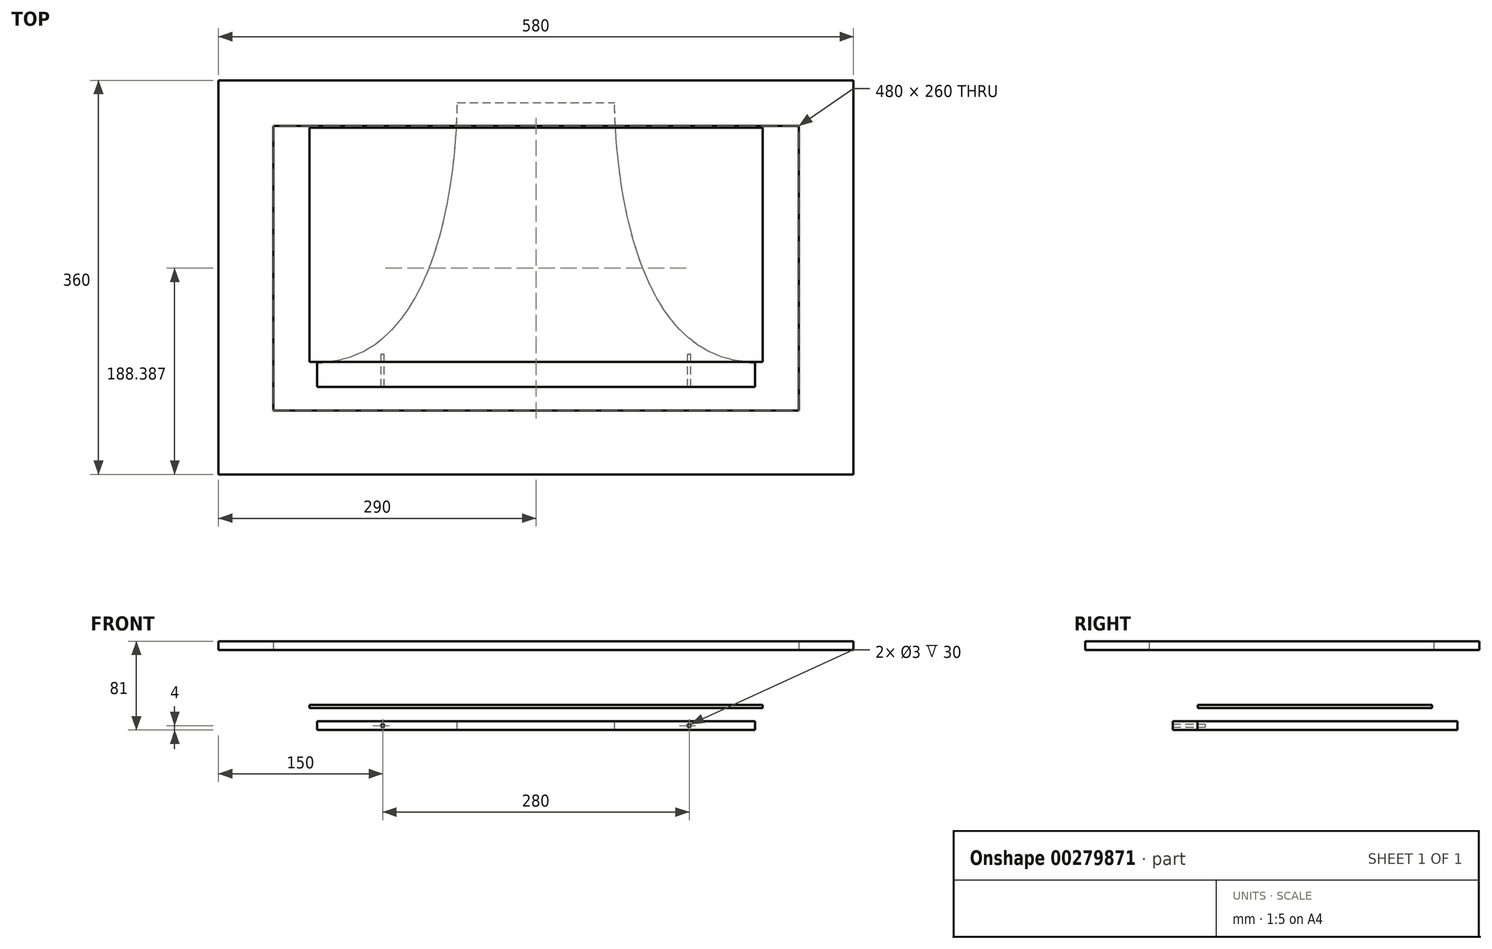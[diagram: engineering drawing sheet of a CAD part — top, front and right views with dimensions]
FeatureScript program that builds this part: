
annotation { "Feature Type Name" : "Feature", "Feature Type Description" : "" }
export const myFeature = defineFeature(function(context is Context, id is Id, definition is map)
    precondition{}
    {
        {
            var Q0;
            Q0=qCreatedBy(makeId("Top.planeOp"),FACE);
            var sketch = newSketch(context, id + "F0", { "sketchPlane" : qUnion([Q0])});
            skLineSegment(sketch, "E0.bottom", {"start": v(0, 0) * mm, "end": v(400, 0) * mm, "construction": true});
            skLineSegment(sketch, "E0.top", {"start": v(0, 200) * mm, "end": v(400, 200) * mm, "construction": true});
            skLineSegment(sketch, "E0.left", {"start": v(0, 0) * mm, "end": v(0, 200) * mm, "construction": true});
            skLineSegment(sketch, "E0.right", {"start": v(400, 0) * mm, "end": v(400, 200) * mm, "construction": true});
            skLineSegment(sketch, "E1.0", {"start": v(-7, -7) * mm, "end": v(-7, 207) * mm});
            skLineSegment(sketch, "E1.1", {"start": v(-7, -7) * mm, "end": v(407, -7) * mm});
            skLineSegment(sketch, "E1.2", {"start": v(407, -7) * mm, "end": v(407, 207) * mm});
            skLineSegment(sketch, "E1.3", {"start": v(-7, 207) * mm, "end": v(407, 207) * mm});
            skSolve(sketch);
        }
        {
            var Q0;
            Q0 = qSketchRegion(id + "F0", true);
            extrude(context, id + "F1", {"entities" : qUnion([Q0]), "oppositeDirection" : true, "depth" : 3 * mm});
        }
        {
            var Q0;
            Q0=qCreatedBy(makeId("Top.planeOp"),FACE);
            cPlane(context, id + "F2", {"entities" : qUnion([Q0]), "cplaneType" : CPlaneType.OFFSET, "offset" : 15 * mm, "oppositeDirection" : true, "width" : 150 * mm, "height" : 150 * mm});
        }
        {
            var Q0;
            Q0=qCreatedBy(id+"F2.planeOp",FACE);
            var sketch = newSketch(context, id + "F3", { "sketchPlane" : qUnion([Q0])});
            skLineSegment(sketch, "E2", {"start": v(200, 233.83) * mm, "end": v(200, -32.05) * mm, "construction": true});
            skLineSegment(sketch, "E3", {"start": v(0, -30) * mm, "end": v(0, -7.26) * mm});
            skLineSegment(sketch, "E4", {"start": v(0, -30) * mm, "end": v(400, -30) * mm});
            skLineSegment(sketch, "E5", {"start": v(400, -30) * mm, "end": v(400, -7.26) * mm});
            skLineSegment(sketch, "E6", {"start": v(128.1, 230) * mm, "end": v(271.9, 230) * mm});
            skFitSpline(sketch, "E7", {"points": [v(0, -7.26) * mm, v(128.1, 230) * mm], "startDerivative": vector(361.88, 0) * mm, "endDerivative": vector(0, 104.18) * mm});
            skFitSpline(sketch, "E8.MirrorCS", {"points": [v(400, -7.26) * mm, v(271.9, 230) * mm], "startDerivative": vector(-361.88, 0) * mm, "endDerivative": vector(0, 104.18) * mm});
            skSolve(sketch);
        }
        {
            var Q0;
            Q0 = qSketchRegion(id + "F3", true);
            extrude(context, id + "F4", {"entities" : qUnion([Q0]), "oppositeDirection" : true, "depth" : 8 * mm});
        }
        {
            var Q0;
            Q0=qCreatedBy(makeId("Front.planeOp"),FACE);
            var sketch = newSketch(context, id + "F5", { "sketchPlane" : qUnion([Q0])});
            skCircle(sketch, "E9", {"center": v(340, -19) * mm, "radius": 1.5 * mm});
            skCircle(sketch, "E10", {"center": v(60, -19) * mm, "radius": 1.5 * mm});
            skLineSegment(sketch, "E11", {"start": v(340, -19) * mm, "end": v(60, -19) * mm, "construction": true});
            skLineSegment(sketch, "E12", {"start": v(200, -15) * mm, "end": v(200, -23) * mm});
            skPoint(sketch, "E13", {"position": v(200, -19) * mm});
            skSolve(sketch);
        }
        {
            var Q0;
            Q0 = qSketchRegion(id + "F5", true);
            extrude(context, id + "F6", {"entities" : qUnion([Q0]), "operationType" : NewBodyOperationType.REMOVE, "endBound" : BoundingType.THROUGH_ALL, "depth" : 25 * mm});
        }
        {
            var Q0;
            Q0=qCreatedBy(makeId("Top.planeOp"),FACE);
            cPlane(context, id + "F7", {"entities" : qUnion([Q0]), "cplaneType" : CPlaneType.OFFSET, "offset" : 50 * mm, "width" : 150 * mm, "height" : 150 * mm});
        }
        {
            var Q0;
            Q0=qCreatedBy(id+"F7.planeOp",FACE);
            var sketch = newSketch(context, id + "F8", { "sketchPlane" : qUnion([Q0])});
            skLineSegment(sketch, "E14", {"start": v(200, 230) * mm, "end": v(200, -30) * mm, "construction": true});
            skLineSegment(sketch, "E15.bottom", {"start": v(490, 250.23) * mm, "end": v(-90, 250.23) * mm});
            skLineSegment(sketch, "E15.top", {"start": v(490, -109.77) * mm, "end": v(-90, -109.77) * mm});
            skLineSegment(sketch, "E15.left", {"start": v(490, 250.23) * mm, "end": v(490, -109.77) * mm});
            skLineSegment(sketch, "E15.right", {"start": v(-90, 250.23) * mm, "end": v(-90, -109.77) * mm});
            skPoint(sketch, "E15.middle", {"position": v(200, 70.23) * mm});
            skLineSegment(sketch, "E16.bottom", {"start": v(440, 208.62) * mm, "end": v(-40, 208.62) * mm});
            skLineSegment(sketch, "E16.top", {"start": v(440, -51.38) * mm, "end": v(-40, -51.38) * mm});
            skLineSegment(sketch, "E16.left", {"start": v(440, 208.62) * mm, "end": v(440, -51.38) * mm});
            skLineSegment(sketch, "E16.right", {"start": v(-40, 208.62) * mm, "end": v(-40, -51.38) * mm});
            skPoint(sketch, "E16.middle", {"position": v(200, 78.62) * mm});
            skSolve(sketch);
        }
        {
            var Q0;
            Q0 = qSketchRegion(id + "F8", true);
            extrude(context, id + "F9", {"entities" : qUnion([Q0]), "depth" : 8 * mm});
        }
    });
